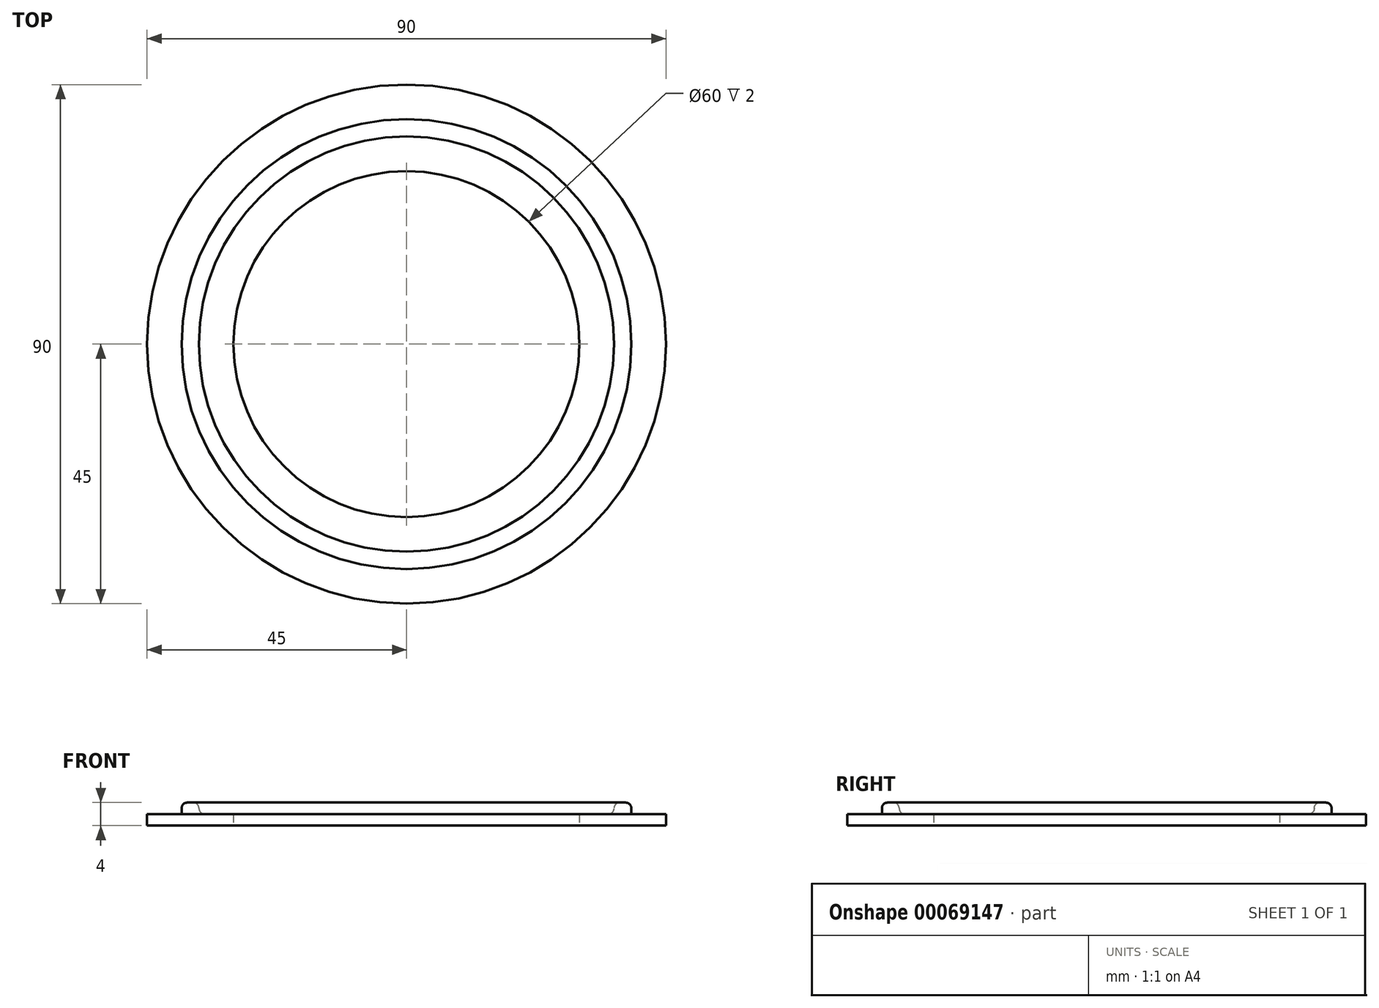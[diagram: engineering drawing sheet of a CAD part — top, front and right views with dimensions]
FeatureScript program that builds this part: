
annotation { "Feature Type Name" : "Feature", "Feature Type Description" : "" }
export const myFeature = defineFeature(function(context is Context, id is Id, definition is map)
    precondition{}
    {
        {
            var Q0;
            Q0=qCreatedBy(makeId("Top.planeOp"),FACE);
            var sketch = newSketch(context, id + "F0", { "sketchPlane" : qUnion([Q0])});
            skCircle(sketch, "E0", {"center": v(0, 0) * mm, "radius": 45 * mm});
            skCircle(sketch, "E1", {"center": v(0, 0) * mm, "radius": 30 * mm});
            skSolve(sketch);
        }
        {
            var Q0;
            Q0 = qSketchRegion(id + "F0", true);
            extrude(context, id + "F1", {"entities" : qUnion([Q0]), "depth" : 2 * mm});
        }
        {
            var Q0;
            Q0=makeQuery(id+"F1.opExtrude","CAP_FACE",FACE,{"disambiguationData":[OSD([sQuery(id+"F0.wireOp",EDGE,"E0"),sQuery(id+"F0.wireOp",EDGE,"E1")])],"isStart":false});
            var sketch = newSketch(context, id + "F2", { "sketchPlane" : qUnion([Q0])});
            skCircle(sketch, "E2", {"center": v(0, 0) * mm, "radius": 39 * mm});
            skCircle(sketch, "E3", {"center": v(0, 0) * mm, "radius": 36 * mm});
            skLineSegment(sketch, "E4", {"start": v(30, 0) * mm, "end": v(45, 0) * mm, "construction": true});
            skPoint(sketch, "E5", {"position": v(37.5, 0) * mm});
            skLineSegment(sketch, "E6", {"start": v(39, 0) * mm, "end": v(36, 0) * mm});
            skSolve(sketch);
        }
        {
            var Q0;
            Q0 = qSketchRegion(id + "F2", true);
            extrude(context, id + "F3", {"entities" : qUnion([Q0]), "operationType" : NewBodyOperationType.ADD, "depth" : 2 * mm});
        }
        {
            var Q0;
            Q0=makeQuery(id+"F3.opExtrude","CAP_EDGE",EDGE,{"disambiguationData":[OSD([sQuery(id+"F2.wireOp",EDGE,"E2")])],"isStart":true});
            var Q1;
            Q1=makeQuery(id+"F3.opExtrude","CAP_EDGE",EDGE,{"disambiguationData":[OSD([sQuery(id+"F2.wireOp",EDGE,"E2")])],"isStart":false});
            var Q2;
            Q2=makeQuery(id+"F3.opExtrude","CAP_EDGE",EDGE,{"disambiguationData":[OSD([sQuery(id+"F2.wireOp",EDGE,"E3")])],"isStart":false});
            var Q3;
            Q3=makeQuery(id+"F3.opExtrude","CAP_EDGE",EDGE,{"disambiguationData":[OSD([sQuery(id+"F2.wireOp",EDGE,"E3")])],"isStart":true});
            fillet(context, id + "F4", {"entities" : qUnion([Q0, Q1, Q2, Q3]), "radius" : 1 * mm, "tangentPropagation" : true, "allowEdgeOverflow" : false});
        }
    });
